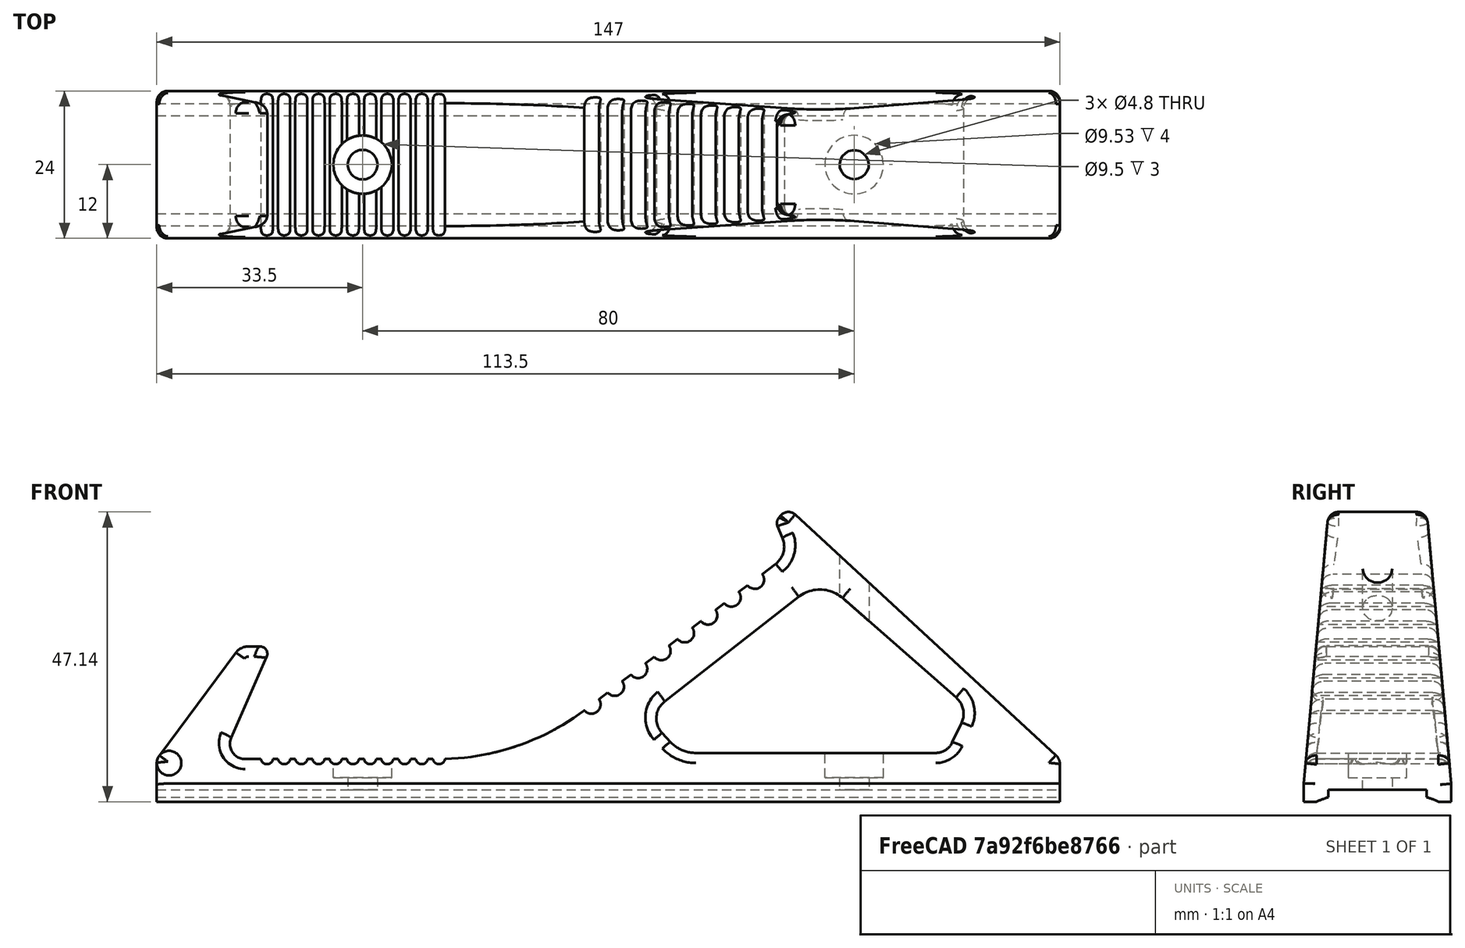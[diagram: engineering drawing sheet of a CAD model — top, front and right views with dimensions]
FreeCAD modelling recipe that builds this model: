
FCSTD DOCUMENT  (FreeCAD 1.1R20260325 (Git shallow))
Label: AngledForeGrip
License: All rights reserved
LicenseURL: https://en.wikipedia.org/wiki/All_rights_reserved
objects: Sketcher::SketchObject×9, PartDesign::Pocket×5, PartDesign::Pad×3, App::Point×2, PartDesign::Fillet×2, Spreadsheet::Sheet×1, Mesh::Feature×1, PartDesign::Body×1, App::Part×1
note: 49 computed .brp shape members not serialized (recipe doc carries the construction recipe); baked Part::Feature solids carry a one-line shape summary decoded from their .brp

FEATURE [Spreadsheet::Sheet] Spreadsheet
  cells = A1='width; B1(width)=16; A2='height; B2(height)=1.2; A3='length; B3(length)=147; A5='diameter; B5(diameter)=50.5; A6='max_width; B6(max_width)=24; B8=1.94; B9=17; A16='mlok_width; B16(mlok_width)=7; A17='mlok_length; B17(mlok_length)=32; A18='mlok_spacing; B18(mlok_spacing)=40; C18='# end to other end
FEATURE [App::Point] Origin001
  Role = Origin
FEATURE [App::Point] Origin003
  Role = Origin
FEATURE [Sketcher::SketchObject] Sketch
  ArcFitTolerance = 1e-06
  AttachmentSupport = -> [Origin002]
  ExternalTypes = [0]
  FullyConstrained = true
  MakeInternals = false
  MapMode = 5
  _ExternalGeoVersion = 1
  expr: Constraints[8] = <<Spreadsheet>>.max_width
  expr: Constraints[9] = <<Spreadsheet>>.length
  sketch-geometry (4):
    g0: LineSegment StartX=-12 StartY=73.5 StartZ=0 EndX=-12 EndY=-73.5 EndZ=0
    g1: LineSegment StartX=-12 StartY=-73.5 StartZ=0 EndX=12 EndY=-73.5 EndZ=0
    g2: LineSegment StartX=12 StartY=-73.5 StartZ=0 EndX=12 EndY=73.5 EndZ=0
    g3: LineSegment StartX=12 StartY=73.5 StartZ=0 EndX=-12 EndY=73.5 EndZ=0
  constraints (11):
    c: Coincident(g0,g1)
    c: Coincident(g1,g2)
    c: Coincident(g2,g3)
    c: Coincident(g3,g0)
    c: Vertical(g0)
    c: Vertical(g2)
    c: Horizontal(g1)
    c: Horizontal(g3)
    c: DistanceX(g3,g3) = 24
    c: DistanceY(g2,g2) = 147
    c: Symmetric(g2,g0,g-1)
FEATURE [PartDesign::Pad] Pad  label="BasePad"
  Direction = (0,0,1)
  Length = 10
  Length2 = 10
  Profile = -> Sketch
  ReferenceAxis = -> Sketch [N_Axis]
  Refine = true
  Reversed = true
  SideType = 0
  Suppressed = false
  Type = 0
  Type2 = 0
FEATURE [Sketcher::SketchObject] Sketch001
  ArcFitTolerance = 1e-06
  AttachmentSupport = -> [Pad]
  ExternalTypes = [0]
  FullyConstrained = true
  MakeInternals = false
  MapMode = 5
  Placement = pos=(0,-73.5,0) rot=(1,0,0;1.5708rad)
  _ExternalGeoVersion = 1
  sketch-geometry (10):
    g0: LineSegment StartX=-8 StartY=-1 StartZ=0 EndX=-8 EndY=-2.2 EndZ=0
    g1: LineSegment StartX=8 StartY=-2.2 StartZ=0 EndX=8 EndY=-1 EndZ=0
    g2: LineSegment StartX=8 StartY=-1 StartZ=0 EndX=-8 EndY=-1 EndZ=0
    g3: ArcOfCircle CenterX=0 CenterY=-26.1492 CenterZ=0 NormalX=0 NormalY=0 NormalZ=1 AngleXU=0 Radius=25.25 StartAngle=1.89318 EndAngle=1.97606
    g4: LineSegment StartX=-16.595 StartY=-2.94441 StartZ=0 EndX=-16.595 EndY=-12.0344 EndZ=0
    g5: LineSegment StartX=-16.595 StartY=-12.0344 StartZ=0 EndX=17.315 EndY=-12.0344 EndZ=0
    g6: LineSegment StartX=17.315 StartY=-12.0344 StartZ=0 EndX=17.315 EndY=-2.94441 EndZ=0
    g7: LineSegment StartX=17.315 StartY=-2.94441 StartZ=0 EndX=9.955 EndY=-2.94441 EndZ=0
    g8: LineSegment StartX=-9.955 StartY=-2.94441 StartZ=0 EndX=-16.595 EndY=-2.94441 EndZ=0
    g9: ArcOfCircle CenterX=0 CenterY=-26.1492 CenterZ=0 NormalX=0 NormalY=0 NormalZ=1 AngleXU=0 Radius=25.25 StartAngle=1.16554 EndAngle=1.24841
  constraints (31):
    c: Coincident(g1,g2)
    c: Coincident(g2,g0)
    c: Vertical(g0)
    c: Vertical(g1)
    c: Horizontal(g2)
    c: Distance(g0,g1) = 16
    c: Distance(g0,g2) = 1.2
    c: DistanceY(g0,g-1) = 1
    c: DistanceX(g0,g-1) = 8
    c: PointOnObject(g3,g-2)
    c: Coincident(g4,g5)
    c: Coincident(g5,g6)
    c: Coincident(g6,g7)
    c: Coincident(g8,g4)
    c: Vertical(g4)
    c: Vertical(g6)
    c: Horizontal(g5)
    c: Horizontal(g7)
    c: Horizontal(g8)
    c: DistanceY(g8,g7) = 0
    c: Coincident(g3,g0)
    c: Coincident(g1,g9)
    c: Diameter(g3) = 50.5
    c: Coincident(g8,g3)
    c: Coincident(g7,g9)
    c: Coincident(g3,g9)
    c: DistanceY(g0,g1) = 0
    c: DistanceX(g5,g5) = 33.91
    c: DistanceX(g7,g7) = 7.36
    c: DistanceX(g8,g8) = 6.64
    c: DistanceY(g4,g4) = 9.09
FEATURE [PartDesign::Pocket] Pocket  label="RailPocket"
  BaseFeature = -> Pad
  Direction = (0,1,-2e-16)
  Length = 5
  Length2 = 5
  Profile = -> Sketch001
  ReferenceAxis = -> Sketch001 [N_Axis]
  Refine = true
  SideType = 0
  Suppressed = false
  Type = 1
  Type2 = 0
FEATURE [Sketcher::SketchObject] Sketch003
  ArcFitTolerance = 1e-06
  ExternalTypes = [0]
  FullyConstrained = true
  MakeInternals = false
  MapMode = 5
  Placement = pos=(0,-3e-16,-1.2) rot=(1,0,0;3.14159rad)
  _ExternalGeoVersion = 1
  sketch-geometry (2):
    g0: Circle CenterX=0 CenterY=-40 CenterZ=0 NormalX=0 NormalY=0 NormalZ=1 AngleXU=0 Radius=2.4
    g1: Circle CenterX=0 CenterY=40 CenterZ=0 NormalX=0 NormalY=0 NormalZ=1 AngleXU=0 Radius=2.4
  constraints (6):
    c: Diameter(g0) = 4.8
    c: PointOnObject(g0,g-2)
    c: Diameter(g1) = 4.8
    c: PointOnObject(g1,g-2)
    c: DistanceY(g-1,g1) = 40
    c: DistanceY(g0,g-1) = 40
FEATURE [Sketcher::SketchObject] Sketch002
  ArcFitTolerance = 1e-06
  AttachmentSupport = -> [Pocket]
  ExternalTypes = [0]
  FullyConstrained = false
  MakeInternals = false
  MapMode = 5
  Placement = pos=(0,-2e-16,-1) rot=(1,0,0;3.14159rad)
  _ExternalGeoVersion = 1
  sketch-geometry (18):
    g0: Circle CenterX=0 CenterY=-40 CenterZ=0 NormalX=0 NormalY=0 NormalZ=1 AngleXU=0 Radius=2.1
    g1: Circle CenterX=0 CenterY=40 CenterZ=0 NormalX=0 NormalY=0 NormalZ=1 AngleXU=0 Radius=2.1
    g2: ArcOfCircle CenterX=0 CenterY=40 CenterZ=0 NormalX=0 NormalY=0 NormalZ=1 AngleXU=0 Radius=3.5 StartAngle=0.5411 EndAngle=2.60049
    g3: ArcOfCircle CenterX=0 CenterY=-40 CenterZ=0 NormalX=0 NormalY=0 NormalZ=1 AngleXU=0 Radius=3.5 StartAngle=0.5411 EndAngle=2.60049
    g4: LineSegment StartX=4.4 StartY=61 StartZ=0 EndX=4.4 EndY=-61 EndZ=0
    g5: LineSegment StartX=4.4 StartY=-61 StartZ=0 EndX=3 EndY=-61 EndZ=0
    g6: LineSegment StartX=3 StartY=-61 StartZ=0 EndX=3 EndY=-41.8028 EndZ=0
    g7: LineSegment StartX=3 StartY=61 StartZ=0 EndX=4.4 EndY=61 EndZ=0
    g8: LineSegment StartX=-3 StartY=61 StartZ=0 EndX=-3 EndY=41.8028 EndZ=0
    g9: LineSegment StartX=-3 StartY=-61 StartZ=0 EndX=-4.4 EndY=-61 EndZ=0
    g10: LineSegment StartX=-4.4 StartY=-61 StartZ=0 EndX=-4.4 EndY=61 EndZ=0
    g11: LineSegment StartX=-4.4 StartY=61 StartZ=0 EndX=-3 EndY=61 EndZ=0
    g12: LineSegment StartX=3 StartY=-38.1972 StartZ=0 EndX=3 EndY=38.1972 EndZ=0
    g13: LineSegment StartX=-3 StartY=-41.8028 StartZ=0 EndX=-3 EndY=-61 EndZ=0
    g14: ArcOfCircle CenterX=0 CenterY=-40 CenterZ=0 NormalX=0 NormalY=0 NormalZ=1 AngleXU=0 Radius=3.5 StartAngle=3.68269 EndAngle=5.74209
    g15: LineSegment StartX=3 StartY=41.8028 StartZ=0 EndX=3 EndY=61 EndZ=0
    g16: LineSegment StartX=-3 StartY=38.1972 StartZ=0 EndX=-3 EndY=-38.1972 EndZ=0
    g17: ArcOfCircle CenterX=0 CenterY=40 CenterZ=0 NormalX=0 NormalY=0 NormalZ=1 AngleXU=0 Radius=3.5 StartAngle=3.68269 EndAngle=5.74209
  constraints (48):
    c: Diameter(g0) = 4.2
    c: PointOnObject(g0,g-2)
    c: Diameter(g1) = 4.2
    c: PointOnObject(g1,g-2)
    c: DistanceY(g-1,g1) = 40
    c: DistanceY(g0,g-1) = 40
    c: Coincident(g2,g1)
    c: Coincident(g3,g0)
    c: Coincident(g4,g5)
    c: Coincident(g5,g6)
    c: Coincident(g15,g7)
    c: Coincident(g7,g4)
    c: Vertical(g4)
    c: Horizontal(g5)
    c: Horizontal(g7)
    c: Distance(g4,g15) = 1.4
    c: Distance(g5,g7) = 122
    c: DistanceY(g-1,g15) = 61
    c: DistanceX(g4,g-1) = -4.4
    c: Coincident(g13,g9)
    c: Coincident(g9,g10)
    c: Coincident(g10,g11)
    c: Coincident(g11,g8)
    c: Vertical(g10)
    c: Horizontal(g9)
    c: Horizontal(g11)
    c: Distance(g8,g10) = 1.4
    c: Distance(g9,g11) = 122
    c: DistanceY(g-1,g10) = 61
    c: DistanceX(g13,g-1) = 3
    c: Vertical(g6)
    c: Coincident(g6,g14)
    c: Coincident(g12,g3)
    c: Vertical(g13)
    c: Diameter(g3) = 7
    c: Coincident(g16,g3)
    c: Coincident(g13,g14)
    c: Coincident(g3,g14)
    c: Vertical(g12)
    c: Vertical(g15)
    c: Coincident(g17,g12)
    c: Coincident(g2,g15)
    c: Vertical(g8)
    c: Vertical(g16)
    c: Diameter(g2) = 7
    c: Coincident(g8,g2)
    c: Coincident(g16,g17)
    c: Coincident(g2,g17)
FEATURE [Sketcher::SketchObject] Sketch004
  ArcFitTolerance = 1e-06
  ExternalTypes = [0]
  FullyConstrained = true
  MakeInternals = false
  MapMode = 5
  _ExternalGeoVersion = 1
  expr: Constraints[9] = <<Spreadsheet>>.length
  sketch-geometry (4):
    g0: LineSegment StartX=-12 StartY=73.5 StartZ=0 EndX=-12 EndY=-73.5 EndZ=0
    g1: LineSegment StartX=-12 StartY=-73.5 StartZ=0 EndX=12 EndY=-73.5 EndZ=0
    g2: LineSegment StartX=12 StartY=-73.5 StartZ=0 EndX=12 EndY=73.5 EndZ=0
    g3: LineSegment StartX=12 StartY=73.5 StartZ=0 EndX=-12 EndY=73.5 EndZ=0
  constraints (11):
    c: Coincident(g0,g1)
    c: Coincident(g1,g2)
    c: Coincident(g2,g3)
    c: Coincident(g3,g0)
    c: Vertical(g0)
    c: Vertical(g2)
    c: Horizontal(g1)
    c: Horizontal(g3)
    c: DistanceX(g1,g1) = 24
    c: DistanceY(g2,g2) = 147
    c: Symmetric(g2,g0,g-1)
FEATURE [PartDesign::Pad] Pad002
  BaseFeature = -> Pocket
  Direction = (0,0,1)
  Length = 4
  Length2 = 10
  Profile = -> Sketch004
  ReferenceAxis = -> Sketch004 [N_Axis]
  Refine = true
  SideType = 0
  Suppressed = false
  Type = 0
  Type2 = 0
FEATURE [Mesh::Feature] M_LOK_AFG_v3  label="M-LOK_AFG_v3"
FEATURE [Sketcher::SketchObject] Sketch005
  ArcFitTolerance = 1e-06
  AttachmentSupport = -> [Pad002]
  ExternalTypes = [0]
  FullyConstrained = false
  MakeInternals = false
  MapMode = 5
  Placement = pos=(12,0,0) rot=(0.57735,0.57735,0.57735;2.0944rad)
  _ExternalGeoVersion = 1
  expr: Constraints[8] = <<Spreadsheet>>.length
  expr: Constraints[9] = <<Spreadsheet>>.length / 2
  sketch-geometry (39):
    g0: LineSegment StartX=-73.5 StartY=0 StartZ=0 EndX=-73.5 EndY=4 EndZ=0
    g1: LineSegment StartX=-73.5 StartY=4 StartZ=0 EndX=-60.6622 EndY=21.264 EndZ=0
    g2: LineSegment StartX=-58.562 StartY=22.3195 StartZ=0 EndX=-56.701 EndY=22.3195 EndZ=0
    g3: LineSegment StartX=-55.6081 StartY=20.6486 StartZ=0 EndX=-61.3778 EndY=7.45627 EndZ=0
    g4: LineSegment StartX=-59.117 StartY=4 StartZ=0 EndX=-27.7043 EndY=4 EndZ=0
    g5: LineSegment StartX=73.5 StartY=4 StartZ=0 EndX=73.5 EndY=0 EndZ=0
    g6: LineSegment StartX=73.5 StartY=0 StartZ=0 EndX=-73.5 EndY=0 EndZ=0
    g7: LineSegment StartX=73.5 StartY=4 StartZ=0 EndX=30.4141 EndY=43.7651 EndZ=0
    g8: LineSegment StartX=28.0134 StartY=43.5814 StartZ=0 EndX=27.6987 EndY=43.1864 EndZ=0
    g9: LineSegment StartX=27.5219 StartY=41.9184 StartZ=0 EndX=28.3389 EndY=39.9622 EndZ=0
    g10: LineSegment StartX=27.2087 StartY=35.7312 StartZ=0 EndX=-3.58845 EndY=12.1676 EndZ=0
    g11: LineSegment StartX=30.9391 StartY=30.3775 StartZ=0 EndX=9.14347 EndY=13.349 EndZ=0
    g12: LineSegment StartX=14.2098 StartY=5 StartZ=0 EndX=53.2583 EndY=5 EndZ=0
    g13: LineSegment StartX=38.1633 StartY=30.1717 StartZ=0 EndX=56.638 EndY=13.9619 EndZ=0
    g14: ArcOfCircle CenterX=-58.562 CenterY=19.7023 CenterZ=0 NormalX=0 NormalY=0 NormalZ=1 AngleXU=0 Radius=2.61717 StartAngle=1.5708 EndAngle=2.50219
    g15: GeomPoint [constr] X=-59.8773 Y=22.3195 Z=0
    g16: ArcOfCircle CenterX=-56.701 CenterY=21.1266 CenterZ=0 NormalX=0 NormalY=0 NormalZ=1 AngleXU=0 Radius=1.19287 StartAngle=5.8709 EndAngle=7.85398
    g17: GeomPoint [constr] X=-54.8773 Y=22.3195 Z=0
    g18: ArcOfCircle CenterX=-59.117 CenterY=6.46752 CenterZ=0 NormalX=0 NormalY=0 NormalZ=1 AngleXU=0 Radius=2.46752 StartAngle=2.72931 EndAngle=4.71239
    g19: ArcOfCircle CenterX=25.0291 CenterY=38.5799 CenterZ=0 NormalX=0 NormalY=0 NormalZ=1 AngleXU=0 Radius=3.58691 StartAngle=5.3655 EndAngle=6.67882
    g20: GeomPoint [constr] X=29.4044 Y=37.4111 Z=0
    g21: ArcOfCircle CenterX=28.682 CenterY=42.403 CenterZ=0 NormalX=0 NormalY=0 NormalZ=1 AngleXU=0 Radius=1.25725 StartAngle=2.46885 EndAngle=3.53722
    g22: GeomPoint [constr] X=27.2353 Y=42.6047 Z=0
    g23: ArcOfCircle CenterX=29.2991 CenterY=42.5571 CenterZ=0 NormalX=0 NormalY=0 NormalZ=1 AngleXU=0 Radius=1.6439 StartAngle=0.825459 EndAngle=2.46885
    g24: GeomPoint [constr] X=29.115 Y=44.964 Z=0
    g25: ArcOfCircle CenterX=34.4269 CenterY=25.9132 CenterZ=0 NormalX=0 NormalY=0 NormalZ=1 AngleXU=0 Radius=5.6652 StartAngle=0.850606 EndAngle=2.23402
    g26: GeomPoint [constr] X=34.6365 Y=33.2661 Z=0
    g27: LineSegment StartX=57.4809 StartY=9.88842 StartZ=0 EndX=55.9808 EndY=6.72261 EndZ=0
    g28: ArcOfCircle CenterX=54.361 CenterY=11.3668 CenterZ=0 NormalX=0 NormalY=0 NormalZ=1 AngleXU=0 Radius=3.45239 StartAngle=5.84067 EndAngle=7.13379
    g29: GeomPoint [constr] X=58.5967 Y=12.2432 Z=0
    g30: ArcOfCircle CenterX=53.2583 CenterY=8.01267 CenterZ=0 NormalX=0 NormalY=0 NormalZ=1 AngleXU=0 Radius=3.01267 StartAngle=4.71239 EndAngle=5.84067
    g31: GeomPoint [constr] X=55.1645 Y=5 Z=0
    g32: LineSegment StartX=10.1018 StartY=6.77732 StartZ=0 EndX=8.74902 EndY=8.21742 EndZ=0
    g33: ArcOfCircle CenterX=14.2098 CenterY=10.6363 CenterZ=0 NormalX=0 NormalY=0 NormalZ=1 AngleXU=0 Radius=5.63626 StartAngle=3.89574 EndAngle=4.71239
    g34: GeomPoint [constr] X=11.7713 Y=5 Z=0
    g35: ArcOfCircle CenterX=11.2887 CenterY=10.6031 CenterZ=0 NormalX=0 NormalY=0 NormalZ=1 AngleXU=0 Radius=3.48453 StartAngle=2.23402 EndAngle=3.89574
    g36: GeomPoint [constr] X=6.13588 Y=10.9992 Z=0
    g37: ArcOfCircle CenterX=-27.7043 CenterY=43.6865 CenterZ=0 NormalX=0 NormalY=0 NormalZ=1 AngleXU=0 Radius=39.6865 StartAngle=4.71239 EndAngle=5.3655
    g38: GeomPoint [constr] X=-14.2633 Y=4 Z=0
  constraints (64):
    c: PointOnObject(g0,g-1)
    c: Vertical(g0)
    c: Coincident(g0,g1)
    c: Horizontal(g4)
    c: Vertical(g5)
    c: Coincident(g5,g6)
    c: Coincident(g6,g0)
    c: Horizontal(g6)
    c: DistanceX(g6,g6) = 147
    c: DistanceX(g0,g-1) = 73.5
    c: DistanceY(g5,g5) = 4
    c: DistanceY(g0,g0) = 4
    c: DistanceY(g17,g15) = 0
    c: DistanceX(g15,g17) = 5
    c: Coincident(g5,g7)
    c: PointOnObject(g15,g1)
    c: PointOnObject(g15,g2)
    c: Tangent(g1,g14) = 1.5708
    c: Tangent(g2,g14) = 1.5708
    c: PointOnObject(g17,g2)
    c: PointOnObject(g17,g3)
    c: Tangent(g2,g16) = 1.5708
    c: Tangent(g3,g16) = 1.5708
    c: Tangent(g3,g18) = -1.5708
    c: Tangent(g4,g18) = -1.5708
    c: PointOnObject(g20,g9)
    c: Tangent(g10,g19) = 1.5708
    c: Tangent(g9,g19) = 1.5708
    c: PointOnObject(g22,g9)
    c: PointOnObject(g22,g8)
    c: Tangent(g9,g21) = -1.5708
    c: Tangent(g8,g21) = -1.5708
    c: PointOnObject(g24,g8)
    c: PointOnObject(g24,g7)
    c: Tangent(g8,g23) = -1.5708
    c: Tangent(g7,g23) = -1.5708
    c: Tangent(g11,g25) = -1.5708
    c: Tangent(g13,g25) = 1.5708
    c: PointOnObject(g20,g10)
    c: PointOnObject(g26,g13)
    c: PointOnObject(g29,g13)
    c: PointOnObject(g29,g27)
    c: Tangent(g13,g28) = 1.5708
    c: Tangent(g27,g28) = 1.5708
    c: PointOnObject(g31,g27)
    c: Tangent(g27,g30) = 1.5708
    c: Tangent(g12,g30) = -1.5708
    c: PointOnObject(g26,g11)
    c: Horizontal(g12)
    c: PointOnObject(g31,g12)
    c: PointOnObject(g34,g32)
    c: PointOnObject(g34,g12)
    c: Tangent(g32,g33) = 1.5708
    c: Tangent(g12,g33) = -1.5708
    c: PointOnObject(g36,g11)
    c: PointOnObject(g36,g32)
    c: Tangent(g11,g35) = -1.5708
    c: Tangent(g32,g35) = 1.5708
    c: DistanceY(g-1,g12) = 5
    c: PointOnObject(g38,g10)
    c: PointOnObject(g38,g4)
    c: Tangent(g10,g37) = 1.5708
    c: Tangent(g4,g37) = -1.5708
    c: DistanceY(g0,g4) = 0
FEATURE [PartDesign::Pad] Pad003
  BaseFeature = -> Pad002
  Direction = (1,0,0)
  Length = 24
  Length2 = 10
  Profile = -> Sketch005
  ReferenceAxis = -> Sketch005 [N_Axis]
  Refine = true
  Reversed = true
  SideType = 0
  Suppressed = false
  Type = 0
  Type2 = 0
FEATURE [Sketcher::SketchObject] Sketch006
  ArcFitTolerance = 1e-06
  AttachmentSupport = -> [Pad003]
  ExternalTypes = [0]
  FullyConstrained = false
  MakeInternals = false
  MapMode = 5
  Placement = pos=(0,73.5,0) rot=(0,0.707107,0.707107;3.14159rad)
  _ExternalGeoVersion = 1
  sketch-geometry (10):
    g0: LineSegment StartX=-19.4846 StartY=47.3213 StartZ=0 EndX=-19.4846 EndY=-9.54765 EndZ=0
    g1: LineSegment StartX=-19.4846 StartY=-9.54765 StartZ=0 EndX=19.023 EndY=-9.54765 EndZ=0
    g2: LineSegment StartX=19.023 StartY=-9.54765 StartZ=0 EndX=19.023 EndY=47.3213 EndZ=0
    g3: LineSegment StartX=19.023 StartY=47.3213 StartZ=0 EndX=-19.4846 EndY=47.3213 EndZ=0
    g4: LineSegment StartX=-12 StartY=0 StartZ=0 EndX=-8 EndY=44.2586 EndZ=0
    g5: LineSegment StartX=-8 StartY=44.2586 StartZ=0 EndX=8 EndY=44.2586 EndZ=0
    g6: LineSegment StartX=8 StartY=44.2586 StartZ=0 EndX=12 EndY=0 EndZ=0
    g7: LineSegment StartX=12 StartY=0 StartZ=0 EndX=15.8134 EndY=-5.35111 EndZ=0
    g8: LineSegment StartX=15.8134 StartY=-5.35111 StartZ=0 EndX=-15.071 EndY=-4.01247 EndZ=0
    g9: LineSegment StartX=-15.071 StartY=-4.01247 StartZ=0 EndX=-12 EndY=0 EndZ=0
  constraints (21):
    c: Coincident(g0,g1)
    c: Coincident(g1,g2)
    c: Coincident(g2,g3)
    c: Coincident(g3,g0)
    c: Vertical(g0)
    c: Vertical(g2)
    c: Horizontal(g1)
    c: Horizontal(g3)
    c: PointOnObject(g4,g-1)
    c: Coincident(g4,g5)
    c: Horizontal(g5)
    c: Coincident(g5,g6)
    c: PointOnObject(g6,g-1)
    c: Coincident(g6,g7)
    c: Coincident(g7,g8)
    c: Coincident(g8,g9)
    c: Coincident(g9,g4)
    c: DistanceX(g4,g6) = 24
    c: DistanceX(g4,g-1) = 12
    c: DistanceX(g5,g5) = 16
    c: DistanceX(g4,g-1) = 8
FEATURE [PartDesign::Pocket] Pocket001
  BaseFeature = -> Pad003
  Direction = (0,-1,2e-16)
  Length = 5
  Length2 = 5
  Profile = -> Sketch006
  ReferenceAxis = -> Sketch006 [N_Axis]
  Refine = true
  SideType = 0
  Suppressed = false
  Type = 1
  Type2 = 0
FEATURE [PartDesign::Pocket] Pocket003
  BaseFeature = -> Pocket001
  Direction = (0,0,1)
  Length = 10
  Length2 = 5
  Profile = -> Sketch003
  ReferenceAxis = -> Sketch003 [N_Axis]
  Refine = true
  SideType = 0
  Suppressed = false
  Type = 1
  Type2 = 0
FEATURE [Sketcher::SketchObject] Sketch008
  ArcFitTolerance = 1e-06
  AttachmentSupport = -> [Pocket003]
  ExternalTypes = [0]
  FullyConstrained = true
  MakeInternals = false
  MapMode = 5
  Placement = pos=(0,0,5) rot=(0,0,1;0rad)
  _ExternalGeoVersion = 1
  sketch-geometry (2):
    g0: Circle CenterX=0 CenterY=-40 CenterZ=0 NormalX=0 NormalY=0 NormalZ=1 AngleXU=0 Radius=4.75
    g1: Circle CenterX=0 CenterY=40 CenterZ=0 NormalX=0 NormalY=0 NormalZ=1 AngleXU=0 Radius=4.765
  constraints (6):
    c: Diameter(g0) = 9.5
    c: PointOnObject(g0,g-2)
    c: Diameter(g1) = 9.53
    c: PointOnObject(g1,g-2)
    c: DistanceY(g-1,g1) = 40
    c: DistanceY(g0,g-1) = 40
FEATURE [PartDesign::Pocket] Pocket004
  BaseFeature = -> Pocket003
  Direction = (0,0,-1)
  Length = 4
  Length2 = 5
  Profile = -> Sketch008
  ReferenceAxis = -> Sketch008 [N_Axis]
  Refine = true
  SideType = 0
  Suppressed = false
  Type = 0
  Type2 = 0
FEATURE [Sketcher::SketchObject] Sketch007
  ArcFitTolerance = 1e-06
  AttachmentSupport = -> [Pocket004]
  ExternalTypes = [0]
  FullyConstrained = false
  MakeInternals = false
  MapMode = 5
  Placement = pos=(12,0,0) rot=(0.57735,0.57735,0.57735;2.0944rad)
  _ExternalGeoVersion = 1
  sketch-geometry (19):
    g0: Circle CenterX=-30.3711 CenterY=4.17541 CenterZ=0 NormalX=0 NormalY=0 NormalZ=1 AngleXU=0 Radius=1
    g1: Circle CenterX=-27.5711 CenterY=4.17541 CenterZ=0 NormalX=0 NormalY=0 NormalZ=1 AngleXU=0 Radius=1
    g2: Circle CenterX=-35.9711 CenterY=4.17541 CenterZ=0 NormalX=0 NormalY=0 NormalZ=1 AngleXU=0 Radius=1
    g3: Circle CenterX=-33.1711 CenterY=4.17541 CenterZ=0 NormalX=0 NormalY=0 NormalZ=1 AngleXU=0 Radius=1
    g4: Circle CenterX=-41.5711 CenterY=4.17541 CenterZ=0 NormalX=0 NormalY=0 NormalZ=1 AngleXU=0 Radius=1
    g5: Circle CenterX=-38.7711 CenterY=4.17541 CenterZ=0 NormalX=0 NormalY=0 NormalZ=1 AngleXU=0 Radius=1
    g6: Circle CenterX=-47.1711 CenterY=4.17541 CenterZ=0 NormalX=0 NormalY=0 NormalZ=1 AngleXU=0 Radius=1
    g7: Circle CenterX=-44.3711 CenterY=4.17541 CenterZ=0 NormalX=0 NormalY=0 NormalZ=1 AngleXU=0 Radius=1
    g8: Circle CenterX=-2.76637 CenterY=12.8798 CenterZ=0 NormalX=0 NormalY=0 NormalZ=1 AngleXU=0 Radius=1.5
    g9: Circle CenterX=1.03363 CenterY=15.7798 CenterZ=0 NormalX=0 NormalY=0 NormalZ=1 AngleXU=0 Radius=1.5
    g10: Circle CenterX=4.83363 CenterY=18.6798 CenterZ=0 NormalX=0 NormalY=0 NormalZ=1 AngleXU=0 Radius=1.5
    g11: Circle CenterX=8.63363 CenterY=21.5798 CenterZ=0 NormalX=0 NormalY=0 NormalZ=1 AngleXU=0 Radius=1.5
    g12: Circle CenterX=12.4336 CenterY=24.4798 CenterZ=0 NormalX=0 NormalY=0 NormalZ=1 AngleXU=0 Radius=1.5
    g13: Circle CenterX=16.2336 CenterY=27.3798 CenterZ=0 NormalX=0 NormalY=0 NormalZ=1 AngleXU=0 Radius=1.5
    g14: Circle CenterX=20.0336 CenterY=30.2798 CenterZ=0 NormalX=0 NormalY=0 NormalZ=1 AngleXU=0 Radius=1.5
    g15: Circle CenterX=23.8336 CenterY=33.1798 CenterZ=0 NormalX=0 NormalY=0 NormalZ=1 AngleXU=0 Radius=1.5
    g16: Circle CenterX=-49.9711 CenterY=4.17541 CenterZ=0 NormalX=0 NormalY=0 NormalZ=1 AngleXU=0 Radius=1
    g17: Circle CenterX=-55.5711 CenterY=4.17541 CenterZ=0 NormalX=0 NormalY=0 NormalZ=1 AngleXU=0 Radius=1
    g18: Circle CenterX=-52.7711 CenterY=4.17541 CenterZ=0 NormalX=0 NormalY=0 NormalZ=1 AngleXU=0 Radius=1
  constraints (53):
    c: Diameter(g0) = 2
    c: Diameter(g1) = 2
    c: Diameter(g2) = 2
    c: Diameter(g3) = 2
    c: Diameter(g4) = 2
    c: Diameter(g5) = 2
    c: Diameter(g6) = 2
    c: Diameter(g7) = 2
    c: DistanceY(g7,g6) = 0
    c: DistanceY(g4,g7) = 0
    c: DistanceY(g5,g4) = 0
    c: DistanceY(g5,g2) = 0
    c: DistanceY(g2,g3) = 0
    c: DistanceY(g3,g0) = 0
    c: DistanceY(g0,g1) = 0
    c: DistanceX(g6,g7) = 2.8
    c: DistanceX(g7,g4) = 2.8
    c: DistanceX(g4,g5) = 2.8
    c: DistanceX(g5,g2) = 2.8
    c: DistanceX(g2,g3) = 2.8
    c: DistanceX(g3,g0) = 2.8
    c: DistanceX(g0,g1) = 2.8
    c: Diameter(g8) = 3
    c: Diameter(g9) = 3
    c: Diameter(g10) = 3
    c: Diameter(g11) = 3
    c: Diameter(g12) = 3
    c: Diameter(g13) = 3
    c: Diameter(g14) = 3
    c: Diameter(g15) = 3
    c: DistanceX(g14,g15) = 3.8
    c: DistanceX(g13,g14) = 3.8
    c: DistanceX(g12,g13) = 3.8
    c: DistanceX(g11,g12) = 3.8
    c: DistanceX(g10,g11) = 3.8
    c: DistanceX(g9,g10) = 3.8
    c: DistanceX(g8,g9) = 3.8
    c: DistanceY(g14,g15) = 2.9
    c: DistanceY(g13,g14) = 2.9
    c: DistanceY(g12,g13) = 2.9
    c: DistanceY(g11,g12) = 2.9
    c: DistanceY(g10,g11) = 2.9
    c: DistanceY(g9,g10) = 2.9
    c: DistanceY(g8,g9) = 2.9
    c: Diameter(g16) = 2
    c: Diameter(g17) = 2
    c: Diameter(g18) = 2
    c: DistanceY(g18,g17) = 0
    c: DistanceY(g16,g18) = 0
    c: DistanceX(g17,g18) = 2.8
    c: DistanceX(g18,g16) = 2.8
    c: DistanceY(g16,g6) = 0
    c: DistanceX(g16,g6) = 2.8
FEATURE [PartDesign::Fillet] Fillet
  Base = -> Pocket004 [Edge70,Edge15,Edge19,Edge45,Edge21,Edge13,Edge83,Edge57]
  BaseFeature = -> Pocket004
  Radius = 1.8
  Refine = true
  SupportTransform = false
  Suppressed = false
  UseAllEdges = false
FEATURE [PartDesign::Fillet] Fillet001
  Base = -> Fillet [Edge12,Edge24]
  BaseFeature = -> Fillet
  Radius = 2
  Refine = true
  SupportTransform = false
  Suppressed = false
  UseAllEdges = false
FEATURE [PartDesign::Pocket] Pocket005
  BaseFeature = -> Fillet001
  Direction = (-1,0,0)
  Length = 5
  Length2 = 5
  Profile = -> Sketch007
  ReferenceAxis = -> Sketch007 [N_Axis]
  Refine = true
  SideType = 0
  Suppressed = false
  Type = 1
  Type2 = 0
FEATURE [PartDesign::Body] Body  label="AngledForeGripBody"
  AllowCompound = true
  Group = -> [Sketch,Pad,Sketch001,Pocket,Sketch002,Sketch003,Sketch004,Pad002,Sketch005,Pad003,Sketch006,Pocket001,Sketch007,Pocket003,Sketch008,Pocket004,Fillet,Fillet001,Pocket005]
  Origin = -> Origin002
  Placement = pos=(0,0,0) rot=(0,0,1;4.71239rad)
  Tip = -> Pocket005
FEATURE [App::Part] Part  label="AngledForeGripPart"
  Group = -> [Body]
  Origin = -> Origin
